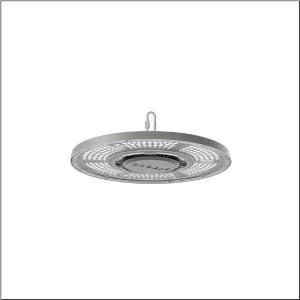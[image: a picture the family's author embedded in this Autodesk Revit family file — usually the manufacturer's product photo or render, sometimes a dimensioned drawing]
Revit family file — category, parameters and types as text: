
# Revit family: highbay_31-s_51hc427a4jmb
name_source: partatom
category: Lighting Fixtures
units: mm (PartAtom-declared; Revit-internal decimal feet)

## family parameters
Cut with Voids When Loaded = No
Host = Face
Light Source = No
Part Type = Normal
Room Calculation Point = No
Round Connector Dimension = Use Diameter
Shared = No

## types (1)
- Highbay 31-S (1 x LED, 20000 lm, 134 W, 4000K)
    Apparent Load = 134 VA
    CIE Flux Codes = 77 99 100 100 100
    Color Rendering = 80
    Color Temperature = 4000K
    Default Elevation = 1800 mm
    Description = Highbay 31-S, LED high bay luminaire, primary light control with lens, of PC, primary optical cover: cover panel, of PC, transparent, light emission: direct distribution, primary light characteristic: rotationally symmetric, installation type: suspended mounting, surface-mounted, LED, rated luminous flux: 20.000lm, luminous efficacy: 150lm/W, light colour: 840, colour temperature: 4000K, control gear: ECG, with cable, 3x 1.0mm², free wire ends, mains connection: 220..240V, AC/DC, 0/50..60Hz, cable length: 1,5m, rated input power: 134W, housing, rotationally symmetric, of diecast aluminium, powder-coated, grey aluminium (RAL 9007), with hook on luminaire side, incl. screw, diameter: 339mm, protection rating (complete): IP65, insulation class (complete): insulation class I (protective earthing), certification: CE, ENEC, UKCA, protection symbol: D, impact resistance: IK08, permissible operating ambient temperature: -30..+45°C, standard: EN 60598-2-22, EN 60598, corresponds to IFS (International Featured Standards) requirements for safety and quality in the food industry, packaging unit: 1 piece
    Height = 141 mm
    Lamp = 1 x LED
    Lamp Light Flux = 20000 lm
    Lamp Power = 134 W
    Lamp count = 1
    Length = 339 mm
    Luminous efficacy = 149 lm/W
    Manufacturer = Siteco
    ModVariant = No
    Model = 51HC427A4JMB
    Mounting Place = Ceiling
    Mounting Type = Pendant
    Number of Poles = 1
    OnlyDefault = Yes
    Power Factor = 1
    Product Name = Highbay 31-S
    Product group = LED high bay luminaire
    ProductGroupID = 903
    Protection Class = Protection class I
    Protection Degree = IP 65
    RLX_Detail_Level = 1
    RLX_Emergency_Light_Flux = 0 lm
    RLX_Emergency_Type = 0
    RLX_Emergency_Type_DB = No
    RlxData = <blob elided: 162661 chars, md5=299178e6>
    Socket = socket
    Standby Power = 0 W
    System Light Flux = 20000 lm
    System Power = 134 W
    Type Comments = Product without accessories
    Type Image = l_1007237.jpg
    URL = http://relux.com
    VarID = ---
    Voltage = 0 V
    Weight = 0.00 kg
    Width = 0 mm  [stored 0 ft]

note: [stored X ft] marks values corroborated as IEEE doubles in the binary element streams (Revit-internal decimal feet)

## geometry (parser evidence)
native form markers: Blend x4, Sweep x8
no freeform markers — native parametric forms only
